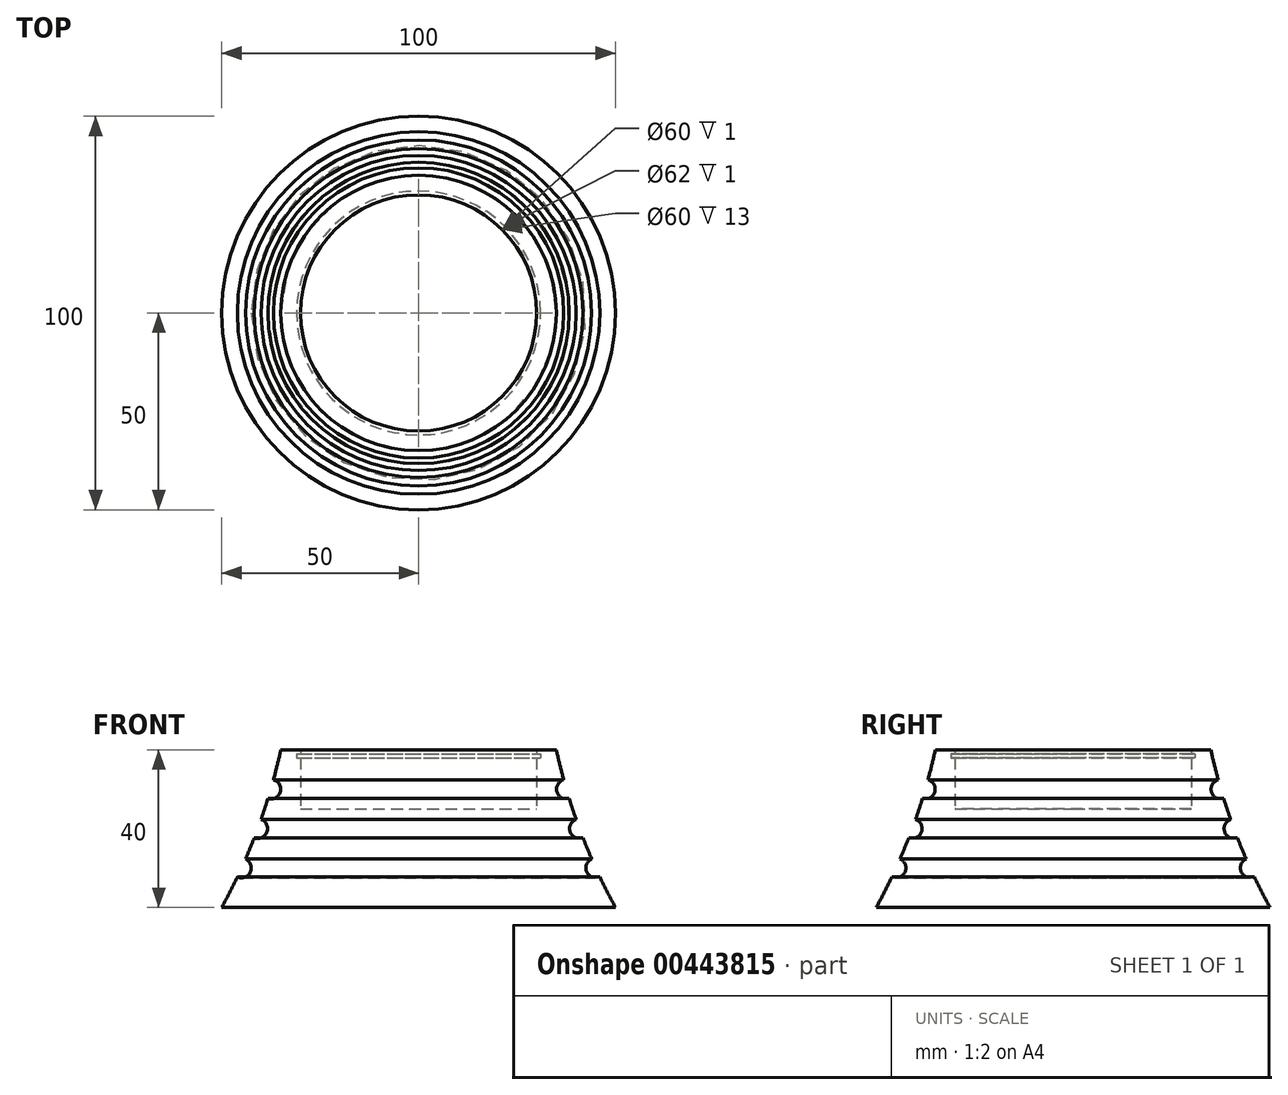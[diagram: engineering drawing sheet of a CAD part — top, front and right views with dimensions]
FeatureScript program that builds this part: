
annotation { "Feature Type Name" : "Feature", "Feature Type Description" : "" }
export const myFeature = defineFeature(function(context is Context, id is Id, definition is map)
    precondition{}
    {
        {
            var Q0;
            Q0=qCreatedBy(makeId("Front.planeOp"),FACE);
            var sketch = newSketch(context, id + "F0", { "sketchPlane" : qUnion([Q0])});
            skLineSegment(sketch, "E0", {"start": v(0, 0) * mm, "end": v(0, 25) * mm});
            skLineSegment(sketch, "E1", {"start": v(0, 25) * mm, "end": v(30, 25) * mm});
            skLineSegment(sketch, "E2", {"start": v(30, 25) * mm, "end": v(30, 38) * mm});
            skLineSegment(sketch, "E3", {"start": v(30, 40) * mm, "end": v(35, 40) * mm});
            skLineSegment(sketch, "E4", {"start": v(0, 0) * mm, "end": v(50, 0) * mm});
            skArc(sketch, "E5", {"start": v(35, 40) * mm, "mid": v(35.89, 36.2) * mm, "end": v(36.87, 32.4) * mm});
            skLineSegment(sketch, "E6.bottom", {"start": v(30, 39) * mm, "end": v(31, 39) * mm});
            skLineSegment(sketch, "E6.top", {"start": v(30, 38) * mm, "end": v(31, 38) * mm});
            skLineSegment(sketch, "E6.right", {"start": v(31, 39) * mm, "end": v(31, 38) * mm});
            skLineSegment(sketch, "E7.trimOffspring", {"start": v(30, 39) * mm, "end": v(30, 40) * mm});
            skArc(sketch, "E8", {"start": v(36.87, 32.4) * mm, "mid": v(35.16, 29.3) * mm, "end": v(38.28, 27.6) * mm});
            skArc(sketch, "E9", {"start": v(43.97, 12.28) * mm, "mid": v(42.72, 8.96) * mm, "end": v(46.05, 7.73) * mm});
            skArc(sketch, "E10", {"start": v(40.02, 22.35) * mm, "mid": v(38.52, 19.13) * mm, "end": v(41.76, 17.66) * mm});
            skArc(sketch, "E11.trimOffspring", {"start": v(46.05, 7.73) * mm, "mid": v(47.97, 3.84) * mm, "end": v(50, 0) * mm});
            skArc(sketch, "E12.trimOffspring", {"start": v(41.76, 17.66) * mm, "mid": v(42.84, 14.96) * mm, "end": v(43.97, 12.28) * mm});
            skArc(sketch, "E13.trimOffspring", {"start": v(38.28, 27.6) * mm, "mid": v(39.12, 24.97) * mm, "end": v(40.02, 22.35) * mm});
            skSolve(sketch);
        }
        {
            var Q0;
            Q0 = qSketchRegion(id + "F0", true);
            var Q1;
            Q1=sQuery(id+"F0.wireOp",EDGE,"E0");
            revolve(context, id + "F1", {"entities" : qUnion([Q0]), "axis" : qUnion([Q1]), "revolveType" : RevolveType.FULL});
        }
    });
